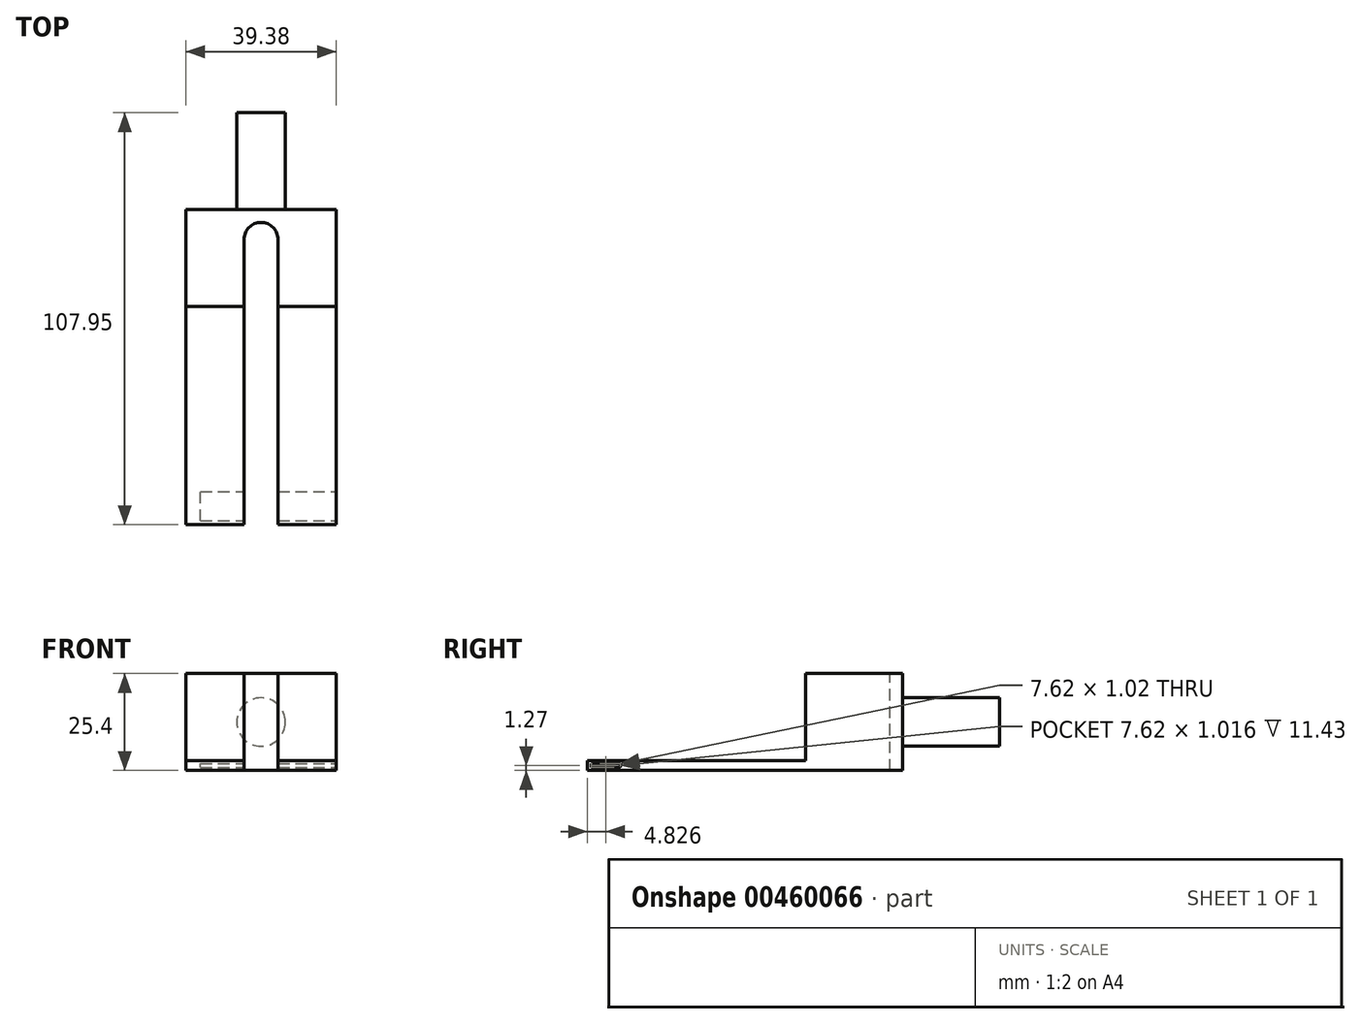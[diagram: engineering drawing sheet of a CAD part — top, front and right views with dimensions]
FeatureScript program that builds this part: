
annotation { "Feature Type Name" : "Feature", "Feature Type Description" : "" }
export const myFeature = defineFeature(function(context is Context, id is Id, definition is map)
    precondition{}
    {
        {
            var Q0;
            Q0=qCreatedBy(makeId("Front.planeOp"),FACE);
            var sketch = newSketch(context, id + "F0", { "sketchPlane" : qUnion([Q0])});
            skCircle(sketch, "E0", {"center": v(0, 0) * mm, "radius": 6.35 * mm});
            skSolve(sketch);
        }
        {
            var Q0;
            Q0 = qSketchRegion(id + "F0", true);
            extrude(context, id + "F1", {"entities" : qUnion([Q0]), "depth" : 25.4 * mm});
        }
        {
            var Q0;
            Q0=makeQuery(id+"F1.opExtrude","CAP_FACE",FACE,{"disambiguationData":[OSD([sQuery(id+"F0.wireOp",EDGE,"E0")])],"isStart":false});
            var sketch = newSketch(context, id + "F2", { "sketchPlane" : qUnion([Q0])});
            skLineSegment(sketch, "E1.bottom", {"start": v(19.69, 12.7) * mm, "end": v(-19.69, 12.7) * mm});
            skLineSegment(sketch, "E1.top", {"start": v(19.68, -12.7) * mm, "end": v(-19.69, -12.7) * mm});
            skLineSegment(sketch, "E1.left", {"start": v(19.68, 12.7) * mm, "end": v(19.68, -12.7) * mm});
            skLineSegment(sketch, "E1.right", {"start": v(-19.69, 12.7) * mm, "end": v(-19.69, -12.7) * mm});
            skPoint(sketch, "E1.middle", {"position": v(0, 0) * mm});
            skSolve(sketch);
        }
        {
            var Q0;
            Q0 = qSketchRegion(id + "F2", true);
            extrude(context, id + "F3", {"entities" : qUnion([Q0]), "operationType" : NewBodyOperationType.ADD, "depth" : 25.4 * mm});
        }
        {
            var Q0;
            Q0=makeQuery(id+"F3.opExtrude","SWEPT_FACE",FACE,{"disambiguationData":[OSD([sQuery(id+"F2.wireOp",EDGE,"E1.bottom")])]});
            var sketch = newSketch(context, id + "F4", { "sketchPlane" : qUnion([Q0])});
            skLineSegment(sketch, "E2.bottom", {"start": v(-4.44, -50.8) * mm, "end": v(4.44, -50.8) * mm});
            skLineSegment(sketch, "E2.top", {"start": v(-4.44, -33.2) * mm, "end": v(4.45, -33.2) * mm});
            skLineSegment(sketch, "E2.left", {"start": v(-4.44, -50.8) * mm, "end": v(-4.44, -33.2) * mm});
            skLineSegment(sketch, "E2.right", {"start": v(4.45, -50.8) * mm, "end": v(4.45, -33.2) * mm});
            skPoint(sketch, "E3.center.orphan", {"position": v(0, -50.8) * mm});
            skCircle(sketch, "E4", {"center": v(0, -33.2) * mm, "radius": 4.45 * mm});
            skSolve(sketch);
        }
        {
            var Q0;
            Q0 = qSketchRegion(id + "F4", true);
            extrude(context, id + "F5", {"entities" : qUnion([Q0]), "operationType" : NewBodyOperationType.REMOVE, "oppositeDirection" : true, "depth" : 25.4 * mm});
        }
        {
            var Q0;
            {var subQ0=sQuery(id+"F2.wireOp",EDGE,"E1.bottom");var subQ1=sQuery(id+"F2.wireOp",EDGE,"E1.top");var subQ2=sQuery(id+"F2.wireOp",EDGE,"E1.left");Q0=makeQuery(id+"F5.boolean.opBoolean","SPLIT",FACE,{"disambiguationData":[TD([makeQuery(id+"F3.opExtrude","SWEPT_FACE",FACE,{"disambiguationData":[OSD([subQ2])]})])],"derivedFrom":makeQuery(id+"F3.opExtrude","CAP_FACE",FACE,{"disambiguationData":[OSD([subQ0,subQ1,subQ2,sQuery(id+"F2.wireOp",EDGE,"E1.right")])],"isStart":false})});}
            var sketch = newSketch(context, id + "F6", { "sketchPlane" : qUnion([Q0])});
            skLineSegment(sketch, "E5.bottom", {"start": v(19.68, -10.16) * mm, "end": v(4.44, -10.16) * mm});
            skLineSegment(sketch, "E5.left", {"start": v(19.68, -10.16) * mm, "end": v(19.68, 12.7) * mm});
            skLineSegment(sketch, "E5.right", {"start": v(4.45, -10.16) * mm, "end": v(4.45, 12.7) * mm});
            skLineSegment(sketch, "E6", {"start": v(4.44, -12.7) * mm, "end": v(19.68, -12.7) * mm});
            skLineSegment(sketch, "E7", {"start": v(-4.44, -10.16) * mm, "end": v(-19.69, -10.16) * mm});
            skLineSegment(sketch, "E8", {"start": v(-19.69, -12.7) * mm, "end": v(-4.44, -12.7) * mm});
            skLineSegment(sketch, "E9", {"start": v(-19.69, -10.16) * mm, "end": v(-19.69, -12.7) * mm});
            skLineSegment(sketch, "E10", {"start": v(-4.44, -10.16) * mm, "end": v(-4.44, -12.7) * mm});
            skLineSegment(sketch, "E11", {"start": v(4.44, -10.16) * mm, "end": v(4.44, -12.7) * mm});
            skLineSegment(sketch, "E12", {"start": v(19.68, -10.16) * mm, "end": v(19.68, -12.7) * mm});
            skSolve(sketch);
        }
        {
            var Q0;
            Q0=makeQuery(id+"F6.imprint","IMPRINT",FACE,{"disambiguationData":[TD([[makeQuery(id+"F6.imprint","IMPRINT",EDGE,{"derivedFrom":sQuery(id+"F6.wireOp",EDGE,"E7")}),1.0]])]});
            var Q1;
            Q1=makeQuery(id+"F6.imprint","IMPRINT",FACE,{"disambiguationData":[TD([[makeQuery(id+"F6.imprint","IMPRINT",EDGE,{"derivedFrom":sQuery(id+"F6.wireOp",EDGE,"E5.bottom")}),1.0]])]});
            extrude(context, id + "F7", {"entities" : qUnion([Q0, Q1]), "operationType" : NewBodyOperationType.ADD, "depth" : 57.15 * mm});
        }
        {
            var Q0;
            Q0=makeQuery(id+"F7.boolean.opBoolean","MERGE",FACE,{"derivedFrom":[makeQuery(id+"F3.opExtrude","SWEPT_FACE",FACE,{"disambiguationData":[OSD([sQuery(id+"F2.wireOp",EDGE,"E1.left")])]}),makeQuery(id+"F7.opExtrude","SWEPT_FACE",FACE,{"disambiguationData":[OSD([sQuery(id+"F6.wireOp",EDGE,"E12")])]})]});
            var sketch = newSketch(context, id + "F8", { "sketchPlane" : qUnion([Q0])});
            skLineSegment(sketch, "E13.bottom", {"start": v(-106.93, -11.94) * mm, "end": v(-99.31, -11.94) * mm});
            skLineSegment(sketch, "E13.top", {"start": v(-106.93, -10.92) * mm, "end": v(-99.31, -10.92) * mm});
            skLineSegment(sketch, "E13.left", {"start": v(-106.93, -11.94) * mm, "end": v(-106.93, -10.92) * mm});
            skLineSegment(sketch, "E13.right", {"start": v(-99.31, -11.94) * mm, "end": v(-99.31, -10.92) * mm});
            skSolve(sketch);
        }
        {
            var Q0;
            Q0 = qSketchRegion(id + "F8", true);
            extrude(context, id + "F9", {"entities" : qUnion([Q0]), "operationType" : NewBodyOperationType.REMOVE, "oppositeDirection" : true, "depth" : 35.56 * mm});
        }
    });
